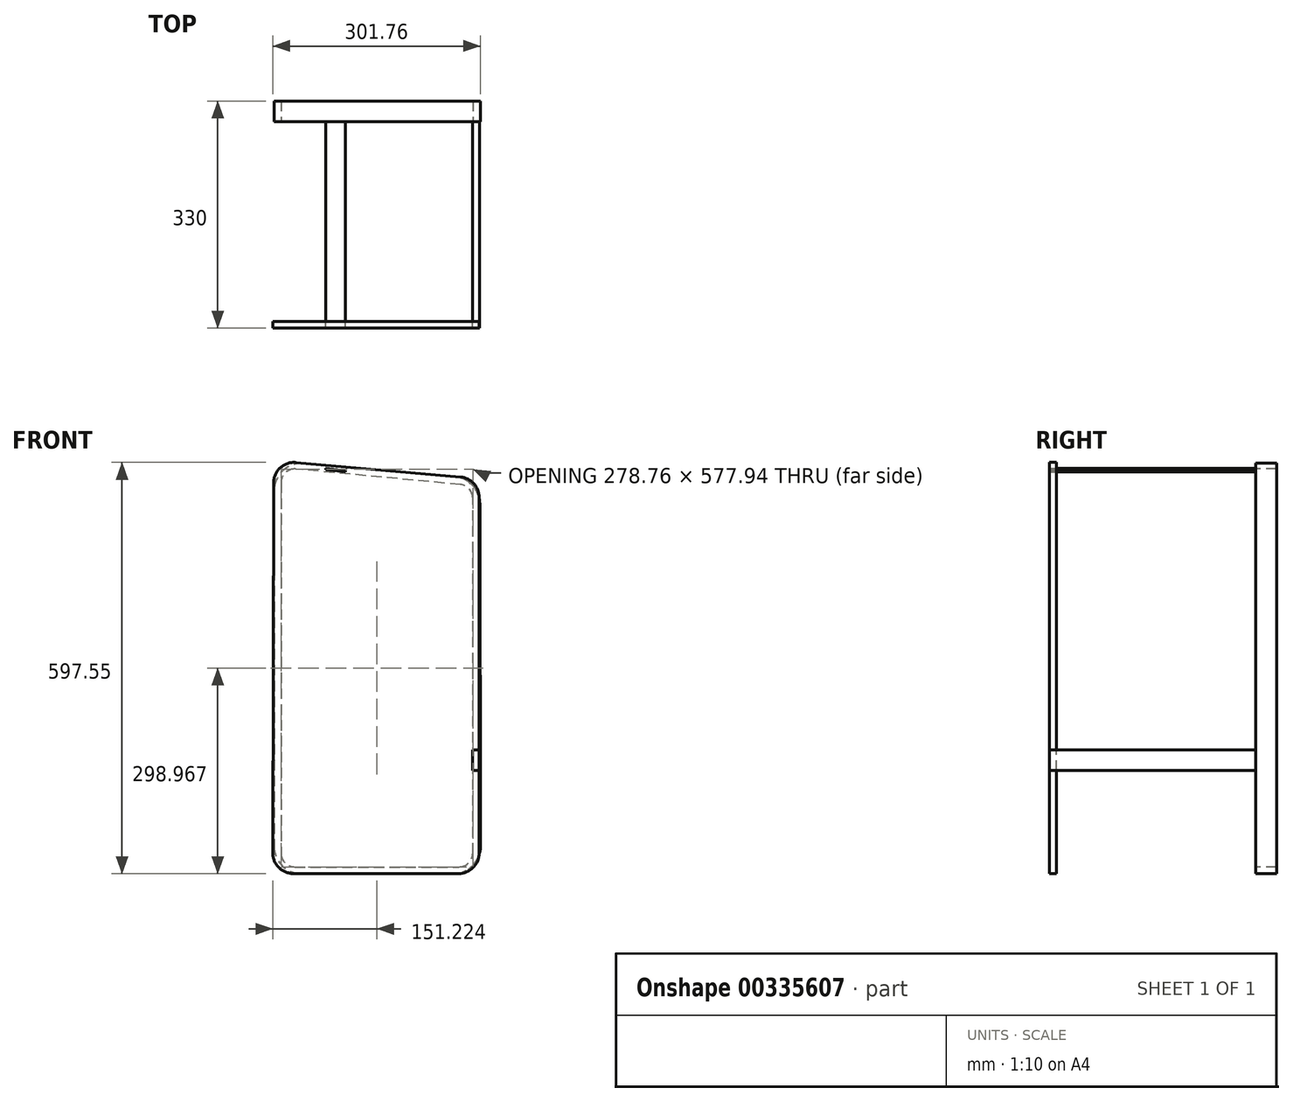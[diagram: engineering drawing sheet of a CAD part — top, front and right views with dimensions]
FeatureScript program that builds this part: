
annotation { "Feature Type Name" : "Feature", "Feature Type Description" : "" }
export const myFeature = defineFeature(function(context is Context, id is Id, definition is map)
    precondition{}
    {
        {
            var Q0;
            Q0=qCreatedBy(makeId("Front.planeOp"),FACE);
            var sketch = newSketch(context, id + "F0", { "sketchPlane" : qUnion([Q0])});
            skLineSegment(sketch, "E0", {"start": v(-156.26, 294.86) * mm, "end": v(-156.26, -221.46) * mm});
            skLineSegment(sketch, "E1", {"start": v(103.66, -261.46) * mm, "end": v(-116.26, -261.46) * mm});
            skLineSegment(sketch, "E2", {"start": v(-112.75, 334.71) * mm, "end": v(106.17, 315.44) * mm});
            skLineSegment(sketch, "E3", {"start": v(142.66, 275.68) * mm, "end": v(143.66, -221.38) * mm});
            skPoint(sketch, "E4.visualSharp", {"position": v(-156.26, 338.54) * mm});
            skArc(sketch, "E4.filletArc", {"start": v(-112.75, 334.71) * mm, "mid": v(-143.27, 324.36) * mm, "end": v(-156.26, 294.86) * mm});
            skPoint(sketch, "E5.visualSharp", {"position": v(142.59, 312.24) * mm});
            skArc(sketch, "E5.filletArc", {"start": v(142.66, 275.68) * mm, "mid": v(132.13, 302.64) * mm, "end": v(106.17, 315.44) * mm});
            skPoint(sketch, "E6.visualSharp", {"position": v(143.74, -261.46) * mm});
            skArc(sketch, "E6.filletArc", {"start": v(103.66, -261.46) * mm, "mid": v(131.97, -249.72) * mm, "end": v(143.66, -221.38) * mm});
            skPoint(sketch, "E7.visualSharp", {"position": v(-156.26, -261.46) * mm});
            skArc(sketch, "E7.filletArc", {"start": v(-156.26, -221.46) * mm, "mid": v(-144.54, -249.75) * mm, "end": v(-116.26, -261.46) * mm});
            skSolve(sketch);
        }
        {
            var Q0;
            Q0 = qSketchRegion(id + "F0", true);
            extrude(context, id + "F1", {"entities" : qUnion([Q0]), "oppositeDirection" : true, "depth" : 30 * mm});
        }
        {
            var Q0;
            Q0=makeQuery(id+"F1.opExtrude","CAP_FACE",FACE,{"disambiguationData":[OSD([sQuery(id+"F0.wireOp",EDGE,"E0"),sQuery(id+"F0.wireOp",EDGE,"E1"),sQuery(id+"F0.wireOp",EDGE,"E2"),sQuery(id+"F0.wireOp",EDGE,"E3"),sQuery(id+"F0.wireOp",EDGE,"E4.filletArc"),sQuery(id+"F0.wireOp",EDGE,"E5.filletArc"),sQuery(id+"F0.wireOp",EDGE,"E6.filletArc"),sQuery(id+"F0.wireOp",EDGE,"E7.filletArc")])],"isStart":true});
            var sketch = newSketch(context, id + "F2", { "sketchPlane" : qUnion([Q0])});
            skLineSegment(sketch, "E8", {"start": v(-146.26, 306.56) * mm, "end": v(-146.26, -231.46) * mm});
            skLineSegment(sketch, "E9", {"start": v(-126.26, -251.46) * mm, "end": v(112.5, -251.46) * mm});
            skLineSegment(sketch, "E10", {"start": v(132.5, -231.46) * mm, "end": v(132.5, 284.04) * mm});
            skLineSegment(sketch, "E11", {"start": v(114.38, 303.95) * mm, "end": v(-124.38, 326.47) * mm});
            skPoint(sketch, "E12.visualSharp", {"position": v(-146.26, 328.54) * mm});
            skArc(sketch, "E12.filletArc", {"start": v(-124.38, 326.47) * mm, "mid": v(-139.72, 321.35) * mm, "end": v(-146.26, 306.56) * mm});
            skPoint(sketch, "E13.visualSharp", {"position": v(132.5, 302.24) * mm});
            skArc(sketch, "E13.filletArc", {"start": v(132.5, 284.04) * mm, "mid": v(127.3, 297.5) * mm, "end": v(114.38, 303.95) * mm});
            skPoint(sketch, "E14.visualSharp", {"position": v(132.5, -251.46) * mm});
            skArc(sketch, "E14.filletArc", {"start": v(112.5, -251.46) * mm, "mid": v(126.65, -245.6) * mm, "end": v(132.5, -231.46) * mm});
            skPoint(sketch, "E15.visualSharp", {"position": v(-146.26, -251.46) * mm});
            skArc(sketch, "E15.filletArc", {"start": v(-146.26, -231.46) * mm, "mid": v(-140.4, -245.6) * mm, "end": v(-126.26, -251.46) * mm});
            skSolve(sketch);
        }
        {
            var Q0;
            Q0 = qSketchRegion(id + "F2", true);
            extrude(context, id + "F3", {"entities" : qUnion([Q0]), "operationType" : NewBodyOperationType.REMOVE, "oppositeDirection" : true, "depth" : 30 * mm});
        }
        {
            var Q0;
            Q0=qCreatedBy(makeId("Front.planeOp"),FACE);
            var sketch = newSketch(context, id + "F4", { "sketchPlane" : qUnion([Q0])});
            skLineSegment(sketch, "E16.bottom", {"start": v(132.36, -81.46) * mm, "end": v(142.36, -81.46) * mm});
            skLineSegment(sketch, "E16.top", {"start": v(132.36, -111.46) * mm, "end": v(142.36, -111.46) * mm});
            skLineSegment(sketch, "E16.left", {"start": v(132.36, -81.46) * mm, "end": v(132.36, -111.46) * mm});
            skLineSegment(sketch, "E16.right", {"start": v(142.36, -81.46) * mm, "end": v(142.36, -111.46) * mm});
            skSolve(sketch);
        }
        {
            var Q0;
            Q0 = qSketchRegion(id + "F4", true);
            extrude(context, id + "F5", {"entities" : qUnion([Q0]), "depth" : 300 * mm});
        }
        {
            var Q0;
            Q0=qCreatedBy(makeId("Front.planeOp"),FACE);
            var sketch = newSketch(context, id + "F6", { "sketchPlane" : qUnion([Q0])});
            skLineSegment(sketch, "E17", {"start": v(-81.26, 327.24) * mm, "end": v(-81.26, 325.24) * mm});
            skLineSegment(sketch, "E18", {"start": v(-81.26, 325.24) * mm, "end": v(-52.4, 322.35) * mm});
            skLineSegment(sketch, "E19", {"start": v(-52.4, 322.35) * mm, "end": v(-52.4, 324.35) * mm});
            skLineSegment(sketch, "E20", {"start": v(-52.4, 324.35) * mm, "end": v(-81.26, 327.24) * mm});
            skSolve(sketch);
        }
        {
            var Q0;
            Q0 = qSketchRegion(id + "F6", true);
            extrude(context, id + "F7", {"entities" : qUnion([Q0]), "operationType" : NewBodyOperationType.ADD, "depth" : 300 * mm});
        }
        {
            var Q0;
            Q0=makeQuery(id+"F5.opExtrude","CAP_FACE",FACE,{"disambiguationData":[OSD([sQuery(id+"F4.wireOp",EDGE,"E16.bottom"),sQuery(id+"F4.wireOp",EDGE,"E16.top"),sQuery(id+"F4.wireOp",EDGE,"E16.left"),sQuery(id+"F4.wireOp",EDGE,"E16.right")])],"isStart":false});
            var sketch = newSketch(context, id + "F8", { "sketchPlane" : qUnion([Q0])});
            skLineSegment(sketch, "E21", {"start": v(-128.1, -261.15) * mm, "end": v(111.84, -261.15) * mm});
            skLineSegment(sketch, "E22", {"start": v(141.84, -231.15) * mm, "end": v(141.84, 285.07) * mm});
            skLineSegment(sketch, "E23", {"start": v(114.47, 314.95) * mm, "end": v(-124.43, 335.98) * mm});
            skLineSegment(sketch, "E24", {"start": v(-157.06, 306.15) * mm, "end": v(-158.1, -231.1) * mm});
            skPoint(sketch, "E25.visualSharp", {"position": v(-157, 338.85) * mm});
            skArc(sketch, "E25.filletArc", {"start": v(-124.43, 335.98) * mm, "mid": v(-147.3, 328.24) * mm, "end": v(-157.06, 306.15) * mm});
            skPoint(sketch, "E26.visualSharp", {"position": v(141.84, 312.55) * mm});
            skArc(sketch, "E26.filletArc", {"start": v(141.84, 285.07) * mm, "mid": v(133.97, 305.33) * mm, "end": v(114.47, 314.95) * mm});
            skPoint(sketch, "E27.visualSharp", {"position": v(141.84, -261.15) * mm});
            skArc(sketch, "E27.filletArc", {"start": v(111.84, -261.15) * mm, "mid": v(133.06, -252.37) * mm, "end": v(141.84, -231.15) * mm});
            skPoint(sketch, "E28.visualSharp", {"position": v(-158.16, -261.15) * mm});
            skArc(sketch, "E28.filletArc", {"start": v(-158.1, -231.1) * mm, "mid": v(-149.33, -252.35) * mm, "end": v(-128.1, -261.15) * mm});
            skSolve(sketch);
        }
        {
            var Q0;
            Q0 = qSketchRegion(id + "F8", true);
            extrude(context, id + "F9", {"entities" : qUnion([Q0]), "oppositeDirection" : true, "depth" : 10 * mm});
        }
    });
